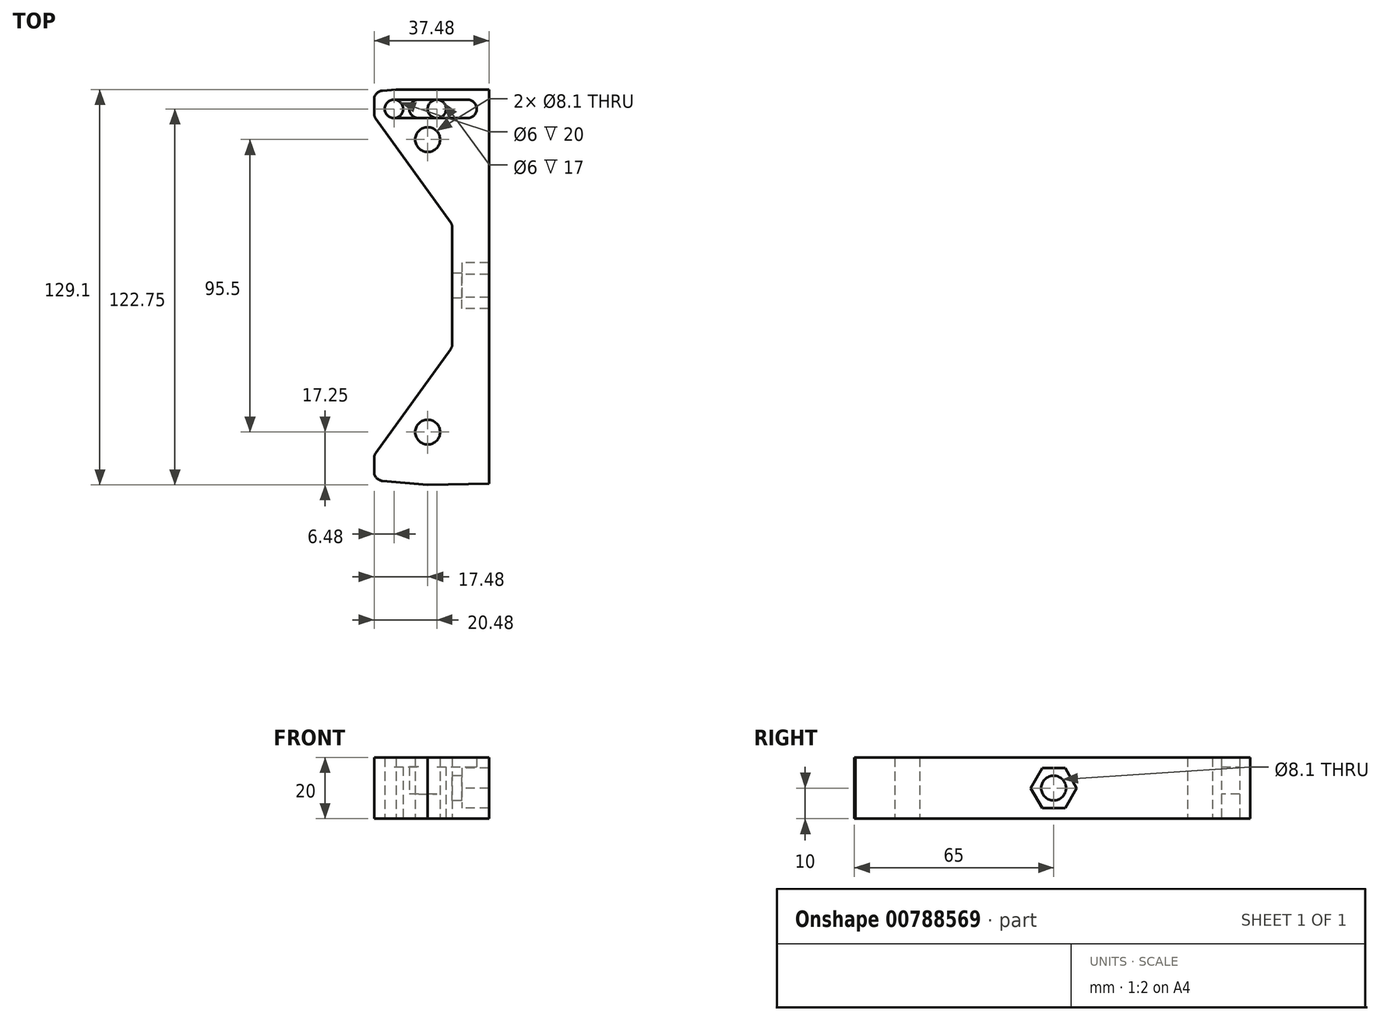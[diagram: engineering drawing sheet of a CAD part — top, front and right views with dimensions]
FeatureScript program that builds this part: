
annotation { "Feature Type Name" : "Feature", "Feature Type Description" : "" }
export const myFeature = defineFeature(function(context is Context, id is Id, definition is map)
    precondition{}
    {
        {
            var Q0;
            Q0=qCreatedBy(makeId("Top.planeOp"),FACE);
            var sketch = newSketch(context, id + "F0", { "sketchPlane" : qUnion([Q0])});
            skCircle(sketch, "E0", {"center": v(0, 0) * mm, "radius": 55 * mm});
            skLineSegment(sketch, "E1", {"start": v(0, 0) * mm, "end": v(126.3, 126.3) * mm, "construction": true});
            skLineSegment(sketch, "E2.MirrorCS", {"start": v(0, 0) * mm, "end": v(-126.3, 126.3) * mm, "construction": true});
            skLineSegment(sketch, "E3.MirrorCS", {"start": v(0, 0) * mm, "end": v(-126.3, -126.3) * mm, "construction": true});
            skLineSegment(sketch, "E4.MirrorCS", {"start": v(0, 0) * mm, "end": v(126.3, -126.3) * mm, "construction": true});
            skCircle(sketch, "E5", {"center": v(-45.96, 45.96) * mm, "radius": 4 * mm});
            skCircle(sketch, "E6.MirrorC", {"center": v(-45.96, -45.96) * mm, "radius": 4 * mm});
            skCircle(sketch, "E7.MirrorC", {"center": v(45.96, 45.96) * mm, "radius": 4 * mm});
            skCircle(sketch, "E8.MirrorC", {"center": v(45.96, -45.96) * mm, "radius": 4 * mm});
            skCircle(sketch, "E9", {"center": v(0, 0) * mm, "radius": 80 * mm});
            skCircle(sketch, "E10", {"center": v(0, 0) * mm, "radius": 92 * mm});
            skLineSegment(sketch, "E11", {"start": v(0, 0) * mm, "end": v(358.76, 0) * mm, "construction": true});
            skCircle(sketch, "E12", {"center": v(139, 0) * mm, "radius": 5 * mm});
            skLineSegment(sketch, "E13", {"start": v(92, 0) * mm, "end": v(92, 123.66) * mm, "construction": true});
            skLineSegment(sketch, "E14.MirrorCS", {"start": v(92, 0) * mm, "end": v(92, -123.66) * mm, "construction": true});
            skCircle(sketch, "E15", {"center": v(92, 47.75) * mm, "radius": 4.05 * mm});
            skCircle(sketch, "E16.MirrorC", {"center": v(92, -47.75) * mm, "radius": 4.05 * mm});
            skLineSegment(sketch, "E17", {"start": v(92, 65) * mm, "end": v(147, 64) * mm});
            skLineSegment(sketch, "E18.MirrorCS", {"start": v(92, -65) * mm, "end": v(147, -64) * mm});
            skFitSpline(sketch, "E19", {"points": [v(92, 65) * mm, v(26.69, 75.42) * mm], "startDerivative": vector(-61.46, 3.75) * mm, "endDerivative": vector(-62.19, 17.08) * mm});
            skFitSpline(sketch, "E20.MirrorCS", {"points": [v(92, -65) * mm, v(26.69, -75.42) * mm], "startDerivative": vector(-61.46, -3.75) * mm, "endDerivative": vector(-62.19, -17.08) * mm});
            skLineSegment(sketch, "E21", {"start": v(147, 64) * mm, "end": v(147, -64) * mm});
            skCircle(sketch, "E22", {"center": v(0, 0) * mm, "radius": 128 * mm, "construction": true});
            skLineSegment(sketch, "E23", {"start": v(0, 0) * mm, "end": v(0, -157.7) * mm, "construction": true});
            skCircle(sketch, "E24", {"center": v(0, 138) * mm, "radius": 11.5 * mm});
            skCircle(sketch, "E25", {"center": v(0, 118) * mm, "radius": 11.5 * mm});
            skLineSegment(sketch, "E26", {"start": v(-11.5, 138) * mm, "end": v(-11.5, 118) * mm});
            skLineSegment(sketch, "E27.bottom", {"start": v(-30, 158) * mm, "end": v(30, 158) * mm});
            skLineSegment(sketch, "E27.top", {"start": v(-30, 98) * mm, "end": v(30, 98) * mm, "construction": true});
            skLineSegment(sketch, "E27.left", {"start": v(-30, 158) * mm, "end": v(-30, 98) * mm, "construction": true});
            skLineSegment(sketch, "E27.right", {"start": v(30, 158) * mm, "end": v(30, 98) * mm, "construction": true});
            skCircle(sketch, "E28", {"center": v(-23.7, 133.5) * mm, "radius": 2.5 * mm});
            skLineSegment(sketch, "E29", {"start": v(-23.7, 158) * mm, "end": v(-23.7, 98) * mm, "construction": true});
            skLineSegment(sketch, "E30", {"start": v(23.7, 158) * mm, "end": v(23.7, 98) * mm, "construction": true});
            skCircle(sketch, "E31", {"center": v(-23.7, 113.5) * mm, "radius": 2.5 * mm});
            skCircle(sketch, "E32", {"center": v(23.7, 122.5) * mm, "radius": 2.5 * mm});
            skCircle(sketch, "E33", {"center": v(23.7, 142.5) * mm, "radius": 2.5 * mm});
            skLineSegment(sketch, "E34", {"start": v(-26.2, 133.5) * mm, "end": v(-26.2, 113.5) * mm});
            skLineSegment(sketch, "E35", {"start": v(-21.2, 133.5) * mm, "end": v(-21.2, 113.5) * mm});
            skLineSegment(sketch, "E36", {"start": v(26.2, 142.5) * mm, "end": v(26.2, 122.5) * mm});
            skLineSegment(sketch, "E37", {"start": v(21.2, 142.5) * mm, "end": v(21.2, 122.5) * mm});
            skLineSegment(sketch, "E38", {"start": v(0, 98) * mm, "end": v(0, 158) * mm, "construction": true});
            skLineSegment(sketch, "E39", {"start": v(-7.8, 128) * mm, "end": v(9.44, 128) * mm, "construction": true});
            skPoint(sketch, "E39.startSnap0", {"position": v(0, 128) * mm});
            skLineSegment(sketch, "E40", {"start": v(0, 0) * mm, "end": v(0, 184.27) * mm, "construction": true});
            skLineSegment(sketch, "E41.0", {"start": v(23.7, 122.5) * mm, "end": v(23.7, 122.5) * mm});
            skLineSegment(sketch, "E41.1", {"start": v(23.7, 122.5) * mm, "end": v(23.7, 142.5) * mm, "construction": true});
            skLineSegment(sketch, "E41.8", {"start": v(-23.7, 113.5) * mm, "end": v(-23.7, 113.5) * mm});
            skLineSegment(sketch, "E41.9", {"start": v(-23.7, 113.5) * mm, "end": v(-23.7, 133.5) * mm, "construction": true});
            skLineSegment(sketch, "E42.0", {"start": v(21.2, 122.5) * mm, "end": v(26.2, 122.5) * mm, "construction": true});
            skLineSegment(sketch, "E43.0", {"start": v(-7.8, 128) * mm, "end": v(0, 128) * mm, "construction": true});
            skLineSegment(sketch, "E44.0", {"start": v(21.2, 142.5) * mm, "end": v(26.2, 142.5) * mm, "construction": true});
            skLineSegment(sketch, "E45.0", {"start": v(-26.2, 113.5) * mm, "end": v(-21.2, 113.5) * mm, "construction": true});
            skLineSegment(sketch, "E46.0", {"start": v(-11.5, 118) * mm, "end": v(0, 118) * mm, "construction": true});
            skLineSegment(sketch, "E47.0", {"start": v(-11.5, 138) * mm, "end": v(0, 138) * mm, "construction": true});
            skLineSegment(sketch, "E48.0", {"start": v(-26.2, 133.5) * mm, "end": v(-21.2, 133.5) * mm, "construction": true});
            skFitSpline(sketch, "E49", {"points": [v(30, 158) * mm, v(117.85, 64.53) * mm], "startDerivative": vector(-10.17, -139.93) * mm, "endDerivative": vector(95.52, -1.41) * mm});
            skLineSegment(sketch, "E50.MirrorCS", {"start": v(11.5, 138) * mm, "end": v(11.5, 118) * mm});
            skLineSegment(sketch, "E51", {"start": v(112, 0) * mm, "end": v(112, 66) * mm});
            skLineSegment(sketch, "E52", {"start": v(112, 66) * mm, "end": v(80, 66) * mm, "construction": true});
            skLineSegment(sketch, "E53", {"start": v(80, 66) * mm, "end": v(80, 0) * mm});
            skLineSegment(sketch, "E54.MirrorCS", {"start": v(80, -66) * mm, "end": v(80, 0) * mm});
            skLineSegment(sketch, "E55.MirrorCS", {"start": v(112, -66) * mm, "end": v(80, -66) * mm, "construction": true});
            skLineSegment(sketch, "E56.MirrorCS", {"start": v(112, 0) * mm, "end": v(112, -66) * mm});
            skCircle(sketch, "E57", {"center": v(124, 0) * mm, "radius": 5 * mm});
            skLineSegment(sketch, "E58", {"start": v(123.93, -5) * mm, "end": v(138.93, -5) * mm});
            skLineSegment(sketch, "E59.MirrorCS", {"start": v(123.93, 5) * mm, "end": v(138.93, 5) * mm});
            skLineSegment(sketch, "E60", {"start": v(0, 106.5) * mm, "end": v(34.82, 106.5) * mm, "construction": true});
            skLineSegment(sketch, "E61", {"start": v(0, 99.5) * mm, "end": v(49.34, 99.5) * mm, "construction": true});
            skLineSegment(sketch, "E62.MirrorCS", {"start": v(0, 99.5) * mm, "end": v(-49.34, 99.5) * mm, "construction": true});
            skCircle(sketch, "E63", {"center": v(35, 99.5) * mm, "radius": 2.5 * mm});
            skCircle(sketch, "E64.MirrorC", {"center": v(-35, 99.5) * mm, "radius": 2.5 * mm});
            skLineSegment(sketch, "E65", {"start": v(-8.21, 94.5) * mm, "end": v(0, 94.5) * mm});
            skCircle(sketch, "E66.MirrorC", {"center": v(-35, 89.5) * mm, "radius": 2.5 * mm});
            skCircle(sketch, "E67.MirrorC", {"center": v(35, 89.5) * mm, "radius": 2.5 * mm});
            skCircle(sketch, "E68", {"center": v(0, 0) * mm, "radius": 20 * mm, "construction": true});
            skCircle(sketch, "E69", {"center": v(0, 118) * mm, "radius": 10 * mm, "construction": true});
            skLineSegment(sketch, "E70", {"start": v(-10, 118) * mm, "end": v(-20.07, 0) * mm, "construction": true});
            skLineSegment(sketch, "E71.MirrorCS", {"start": v(10, 118) * mm, "end": v(20.07, 0) * mm, "construction": true});
            skLineSegment(sketch, "E72", {"start": v(92, 0) * mm, "end": v(92, 20) * mm});
            skLineSegment(sketch, "E73", {"start": v(92, 20) * mm, "end": v(80, 47.75) * mm});
            skLineSegment(sketch, "E74.MirrorCS", {"start": v(92, -20) * mm, "end": v(80, -47.75) * mm});
            skLineSegment(sketch, "E75", {"start": v(92, 0) * mm, "end": v(92, -20) * mm});
            skArc(sketch, "E76", {"start": v(147, -64) * mm, "mid": v(160.66, 0) * mm, "end": v(147, 64) * mm});
            skFitSpline(sketch, "E77", {"points": [v(-80, 0) * mm, v(-30, 158) * mm], "startDerivative": vector(0, 199.53) * mm, "endDerivative": vector(0, 150.5) * mm});
            skArc(sketch, "E78", {"start": v(30, 158) * mm, "mid": v(0, 166.8) * mm, "end": v(-30, 158) * mm});
            skCircle(sketch, "E79", {"center": v(81, 57.75) * mm, "radius": 3 * mm});
            skCircle(sketch, "E80", {"center": v(105, 57.75) * mm, "radius": 3 * mm});
            skLineSegment(sketch, "E81", {"start": v(100, 20) * mm, "end": v(100, 0) * mm});
            skLineSegment(sketch, "E82", {"start": v(80, 47.75) * mm, "end": v(100, 20) * mm});
            skLineSegment(sketch, "E83", {"start": v(80, 47.75) * mm, "end": v(74.52, 55.36) * mm});
            skLineSegment(sketch, "E84", {"start": v(74.52, 55.36) * mm, "end": v(74.52, 63.47) * mm});
            skLineSegment(sketch, "E85", {"start": v(74.52, 63.47) * mm, "end": v(80, 66) * mm});
            skLineSegment(sketch, "E86", {"start": v(92, 65) * mm, "end": v(74.52, 63.47) * mm});
            skLineSegment(sketch, "E87", {"start": v(81, 60.75) * mm, "end": v(105, 60.75) * mm});
            skLineSegment(sketch, "E88", {"start": v(81, 54.75) * mm, "end": v(105, 54.75) * mm});
            skLineSegment(sketch, "E89.MirrorCS", {"start": v(92, -65) * mm, "end": v(74.52, -63.47) * mm});
            skLineSegment(sketch, "E90.MirrorCS", {"start": v(74.52, -55.36) * mm, "end": v(74.52, -63.47) * mm});
            skLineSegment(sketch, "E91.MirrorCS", {"start": v(80, -47.75) * mm, "end": v(74.52, -55.36) * mm});
            skLineSegment(sketch, "E92.MirrorCS", {"start": v(100, -20) * mm, "end": v(100, 0) * mm});
            skLineSegment(sketch, "E93.MirrorCS", {"start": v(80, -47.75) * mm, "end": v(100, -20) * mm});
            skLineSegment(sketch, "E94", {"start": v(112, 64.1) * mm, "end": v(81.74, 64.1) * mm});
            skCircle(sketch, "E95", {"center": v(89, 57.75) * mm, "radius": 3 * mm});
            skCircle(sketch, "E96.MirrorC", {"center": v(95, 57.75) * mm, "radius": 3 * mm});
            skSolve(sketch);
        }
        {
            var Q0;
            Q0=makeQuery(id+"F0.imprint","IMPRINT",FACE,{"disambiguationData":[TD([[makeQuery(id+"F0.imprint","IMPRINT",EDGE,{"derivedFrom":sQuery(id+"F0.wireOp",EDGE,"E15")}),-1.0]])]});
            var Q1;
            {var subQ4=sQuery(id+"F0.wireOp",EDGE,"E90.MirrorCS");Q1=makeQuery(id+"F0.imprint","IMPRINT",FACE,{"disambiguationData":[TD([[makeQuery(id+"F0.imprint","IMPRINT",EDGE,{"derivedFrom":subQ4}),1.0]])]});}
            var Q2;
            {var subQ0=sQuery(id+"F0.wireOp",EDGE,"E83");Q2=makeQuery(id+"F0.imprint","IMPRINT",FACE,{"disambiguationData":[TD([[makeQuery(id+"F0.imprint","IMPRINT",EDGE,{"derivedFrom":subQ0}),-1.0]])]});}
            extrude(context, id + "F1", {"entities" : qUnion([Q0, Q1, Q2]), "depth" : 20 * mm, "offsetDistance" : 25 * mm});
        }
        {
            var Q0;
            {var subQ0=sQuery(id+"F0.wireOp",EDGE,"E80");var subQ1=makeQuery(id+"F0.imprint","INTERSECT",VERTEX,{"derivedFrom":[subQ0,sQuery(id+"F0.wireOp",EDGE,"E87")]});Q0=makeQuery(id+"F0.imprint","IMPRINT",FACE,{"disambiguationData":[TD([[makeQuery(id+"F0.imprint","IMPRINT",EDGE,{"disambiguationData":[TD([[subQ1,-1.0]])],"derivedFrom":subQ0}),1.0]])]});}
            var Q1;
            {var subQ0=sQuery(id+"F0.wireOp",EDGE,"E79");var subQ1=sQuery(id+"F0.wireOp",EDGE,"E53");var subQ2=makeQuery(id+"F0.imprint","INTERSECT",VERTEX,{"disambiguationData":[OD(0.0)],"derivedFrom":[subQ1,subQ0]});Q1=makeQuery(id+"F0.imprint","IMPRINT",FACE,{"disambiguationData":[TD([[makeQuery(id+"F0.imprint","IMPRINT",EDGE,{"disambiguationData":[TD([[subQ2,-1.0]])],"derivedFrom":subQ1}),1.0]])]});}
            var Q2;
            {var subQ0=sQuery(id+"F0.wireOp",EDGE,"E79");var subQ1=sQuery(id+"F0.wireOp",EDGE,"E53");var subQ2=makeQuery(id+"F0.imprint","INTERSECT",VERTEX,{"disambiguationData":[OD(0.0)],"derivedFrom":[subQ1,subQ0]});Q2=makeQuery(id+"F0.imprint","IMPRINT",FACE,{"disambiguationData":[TD([[makeQuery(id+"F0.imprint","IMPRINT",EDGE,{"disambiguationData":[TD([[subQ2,-1.0]])],"derivedFrom":subQ1}),-1.0]])]});}
            var Q3;
            {var subQ0=sQuery(id+"F0.wireOp",EDGE,"E87");var subQ1=sQuery(id+"F0.wireOp",EDGE,"E79");var subQ2=makeQuery(id+"F0.imprint","INTERSECT",VERTEX,{"derivedFrom":[subQ1,subQ0]});Q3=makeQuery(id+"F0.imprint","IMPRINT",FACE,{"disambiguationData":[TD([[makeQuery(id+"F0.imprint","IMPRINT",EDGE,{"disambiguationData":[TD([[subQ2,1.0]])],"derivedFrom":subQ1}),-1.0]])]});}
            var Q4;
            {var subQ0=sQuery(id+"F0.wireOp",EDGE,"E87");var subQ1=sQuery(id+"F0.wireOp",EDGE,"E80");var subQ2=makeQuery(id+"F0.imprint","INTERSECT",VERTEX,{"derivedFrom":[subQ1,subQ0]});Q4=makeQuery(id+"F0.imprint","IMPRINT",FACE,{"disambiguationData":[TD([[makeQuery(id+"F0.imprint","IMPRINT",EDGE,{"disambiguationData":[TD([[subQ2,-1.0]])],"derivedFrom":subQ1}),-1.0]])]});}
            extrude(context, id + "F2", {"entities" : qUnion([Q0, Q1, Q2, Q3, Q4]), "operationType" : NewBodyOperationType.ADD, "depth" : 17 * mm, "offsetDistance" : 25 * mm});
        }
        {
            var Q0;
            Q0=makeQuery(id+"F1.opExtrude","SWEPT_EDGE",EDGE,{"disambiguationData":[OSD([sQuery(id+"F0.wireOp",EDGE,"E90.MirrorCS"),sQuery(id+"F0.wireOp",EDGE,"E91.MirrorCS")])]});
            var Q1;
            Q1=makeQuery(id+"F1.opExtrude","SWEPT_EDGE",EDGE,{"disambiguationData":[OSD([sQuery(id+"F0.wireOp",EDGE,"E89.MirrorCS"),sQuery(id+"F0.wireOp",EDGE,"E90.MirrorCS")])]});
            var Q2;
            Q2=makeQuery(id+"F1.opExtrude","SWEPT_EDGE",EDGE,{"disambiguationData":[OSD([sQuery(id+"F0.wireOp",EDGE,"E92.MirrorCS"),sQuery(id+"F0.wireOp",EDGE,"E93.MirrorCS")])]});
            var Q3;
            Q3=makeQuery(id+"F1.opExtrude","SWEPT_EDGE",EDGE,{"disambiguationData":[OSD([sQuery(id+"F0.wireOp",EDGE,"E81"),sQuery(id+"F0.wireOp",EDGE,"E82")])]});
            var Q4;
            Q4=makeQuery(id+"F1.opExtrude","SWEPT_EDGE",EDGE,{"disambiguationData":[OSD([sQuery(id+"F0.wireOp",EDGE,"E83"),sQuery(id+"F0.wireOp",EDGE,"E84")])]});
            var Q5;
            Q5=makeQuery(id+"F1.opExtrude","SWEPT_EDGE",EDGE,{"disambiguationData":[OSD([sQuery(id+"F0.wireOp",EDGE,"E84"),sQuery(id+"F0.wireOp",EDGE,"E85"),sQuery(id+"F0.wireOp",EDGE,"E86")])]});
            fillet(context, id + "F3", {"entities" : qUnion([Q0, Q1, Q2, Q3, Q4, Q5]), "radius" : 3 * mm, "tangentPropagation" : true, "allowEdgeOverflow" : false});
        }
        {
            var Q0;
            Q0=qCreatedBy(makeId("Right.planeOp"),FACE);
            var sketch = newSketch(context, id + "F4", { "sketchPlane" : qUnion([Q0])});
            skCircle(sketch, "E97.cCircle", {"center": v(0, 10) * mm, "radius": 6.5 * mm, "construction": true});
            skLineSegment(sketch, "E97.0", {"start": v(3.75, 3.5) * mm, "end": v(-3.75, 3.5) * mm});
            skLineSegment(sketch, "E97.1", {"start": v(-3.75, 3.5) * mm, "end": v(-7.5, 10) * mm});
            skLineSegment(sketch, "E97.2", {"start": v(-7.5, 10) * mm, "end": v(-3.75, 16.5) * mm});
            skLineSegment(sketch, "E97.3", {"start": v(-3.75, 16.5) * mm, "end": v(3.75, 16.5) * mm});
            skLineSegment(sketch, "E97.4", {"start": v(3.75, 16.5) * mm, "end": v(7.5, 10) * mm});
            skLineSegment(sketch, "E97.5", {"start": v(7.5, 10) * mm, "end": v(3.75, 3.5) * mm});
            skPoint(sketch, "E97.0.midPoint", {"position": v(0, 3.5) * mm});
            skCircle(sketch, "E98", {"center": v(0, 10) * mm, "radius": 4.05 * mm});
            skSolve(sketch);
        }
        {
            var Q0;
            Q0=makeQuery(id+"F4.imprint","IMPRINT",FACE,{"disambiguationData":[TD([[makeQuery(id+"F4.imprint","IMPRINT",EDGE,{"derivedFrom":sQuery(id+"F4.wireOp",EDGE,"E98")}),1.0]])]});
            extrude(context, id + "F5", {"entities" : qUnion([Q0]), "operationType" : NewBodyOperationType.REMOVE, "depth" : 219.9 * mm, "offsetDistance" : 25 * mm});
        }
        {
            var Q0;
            Q0=makeQuery(id+"F4.imprint","IMPRINT",FACE,{"disambiguationData":[TD([[makeQuery(id+"F4.imprint","IMPRINT",EDGE,{"derivedFrom":sQuery(id+"F4.wireOp",EDGE,"E97.0")}),-1.0]])]});
            extrude(context, id + "F6", {"entities" : qUnion([Q0]), "operationType" : NewBodyOperationType.REMOVE, "depth" : 146.9 * mm, "offsetDistance" : 25 * mm, "hasSecondDirection" : true, "secondDirectionOppositeDirection" : false, "secondDirectionDepth" : 103.2 * mm});
        }
        {
            var Q0;
            {var subQ0=sQuery(id+"F0.wireOp",EDGE,"E95");var subQ1=makeQuery(id+"F0.imprint","INTERSECT",VERTEX,{"derivedFrom":[sQuery(id+"F0.wireOp",EDGE,"E87"),subQ0]});Q0=makeQuery(id+"F0.imprint","IMPRINT",FACE,{"disambiguationData":[TD([[makeQuery(id+"F0.imprint","IMPRINT",EDGE,{"disambiguationData":[TD([[subQ1,1.0]])],"derivedFrom":subQ0}),1.0]])]});}
            var Q1;
            {var subQ0=sQuery(id+"F0.wireOp",EDGE,"E95");var subQ1=sQuery(id+"F0.wireOp",EDGE,"E87");var subQ2=makeQuery(id+"F0.imprint","INTERSECT",VERTEX,{"derivedFrom":[subQ1,subQ0]});Q1=makeQuery(id+"F0.imprint","IMPRINT",FACE,{"disambiguationData":[TD([[makeQuery(id+"F0.imprint","IMPRINT",EDGE,{"disambiguationData":[TD([[subQ2,-1.0]])],"derivedFrom":subQ1}),-1.0]])]});}
            var Q2;
            {var subQ0=sQuery(id+"F0.wireOp",EDGE,"E96.MirrorC");var subQ1=makeQuery(id+"F0.imprint","INTERSECT",VERTEX,{"derivedFrom":[sQuery(id+"F0.wireOp",EDGE,"E87"),subQ0]});Q2=makeQuery(id+"F0.imprint","IMPRINT",FACE,{"disambiguationData":[TD([[makeQuery(id+"F0.imprint","IMPRINT",EDGE,{"disambiguationData":[TD([[subQ1,1.0]])],"derivedFrom":subQ0}),-1.0]])]});}
            var Q3;
            {var subQ0=sQuery(id+"F0.wireOp",EDGE,"E95");var subQ1=sQuery(id+"F0.wireOp",EDGE,"E88");var subQ2=makeQuery(id+"F0.imprint","INTERSECT",VERTEX,{"derivedFrom":[subQ1,subQ0]});Q3=makeQuery(id+"F0.imprint","IMPRINT",FACE,{"disambiguationData":[TD([[makeQuery(id+"F0.imprint","IMPRINT",EDGE,{"disambiguationData":[TD([[subQ2,-1.0]])],"derivedFrom":subQ1}),1.0]])]});}
            extrude(context, id + "F7", {"entities" : qUnion([Q0, Q1, Q2, Q3]), "operationType" : NewBodyOperationType.ADD, "depth" : 8 * mm, "offsetDistance" : 25 * mm});
        }
    });
